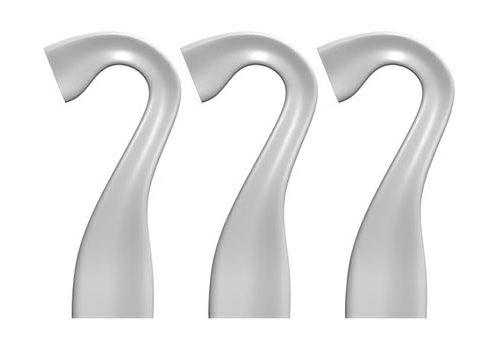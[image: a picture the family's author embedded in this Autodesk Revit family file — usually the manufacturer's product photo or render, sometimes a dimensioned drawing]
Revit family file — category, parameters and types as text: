
# Revit family: CITY ALPHABET letter „M”
name_source: partatom
category: Furniture
revit_build: Autodesk Revit 2018 (Build: 20190510_1515(x64)
units: mm (PartAtom-declared; Revit-internal decimal feet)

## family parameters
Cut with Voids When Loaded = No
Host = Face
OmniClass Number = 23.40.10.11.14
OmniClass Title = Exterior Seating
Room Calculation Point = No
Shared = No

## types (1)
- CITY ALPHABET letter „M”
    Default Elevation = 1219 mm
    Height = 420 mm  [stored 1.37795 ft]
    IfcExportAs = IfcFurnishingElement
    Length = 3350 mm  [stored 10.9908 ft]
    Manufacturer = Astrini Design
    Material information = Colour choice from RAL colour standard. Customer may inquire about specific request regarding individual order.
    Model = CITY ALPHABET letter „M”
    Operating temperature = -40°C to 80°C, ( -40°F to 176°F )
    Type Comments = Bench
    Type Image = M.jpg
    URL = https://astrini-design.pl
    Weight (approximately) = 103.50 kg
    Weight - filled (approximately) = 254.00 kg
    Width = 2350 mm

note: [stored X ft] marks values corroborated as IEEE doubles in the binary element streams (Revit-internal decimal feet)
